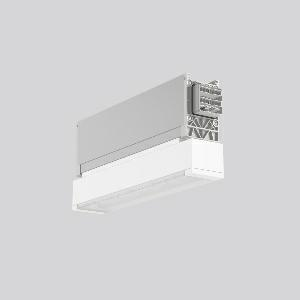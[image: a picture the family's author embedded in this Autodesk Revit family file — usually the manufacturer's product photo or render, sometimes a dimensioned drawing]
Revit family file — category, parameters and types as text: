
# Revit family: linedo_module_rq_9503rq_760_400_0hc_16c4
name_source: partatom
category: Lighting Fixtures
units: mm (PartAtom-declared; Revit-internal decimal feet)

## family parameters
Cut with Voids When Loaded = No
Host = Face
Light Source = No
Part Type = Normal
Room Calculation Point = No
Round Connector Dimension = Use Diameter
Shared = No

## types (1)
- LINEDO Module RQ (1 x LED Modul 763, 390 lm, 6300)
    Apparent Load = 6 VA
    CIE Flux Codes = 39 72 97 99 100
    Color Rendering = 70
    Color Temperature = 6300
    Default Elevation = 1800 mm
    Description = LINEDO, 5,5 W, 390 lm, 763, aluminium, on/off
Continuous line luminaire, L 342 B 58 H 147, CBS, emergency-390 lm, Stromkreis
Project solution!
    Height = 147 mm
    Lamp = 1 x LED Modul 763
    Lamp Light Flux = 390 lm
    Lamp count = 1
    Length = 342 mm
    Lifetime = 50000 h
    Luminous efficacy = 71 lm/W
    Manufacturer = RZB
    ModVariant = No
    Model = 9503RQ.760.400.0HC
    Mounting Place = Ceiling
    Mounting Type = Surface mounted
    Number of Poles = 1
    OnlyDefault = Yes
    Power Factor = 1
    Product Name = LINEDO Module RQ
    Product group = Continuous line luminaire system Linedo IP 54
    ProductGroupID = 314
    Protection Class = Protection class I
    Protection Degree = IP 54
    RLX_Detail_Level = 1
    RLX_Emergency_Light_Flux = 390 lm
    RLX_Emergency_Type = 3
    RLX_Emergency_Type_DB = Yes
    RlxData = <blob elided: 34273 chars, md5=7489cbff>
    Socket = socket
    Standby Power = 0 W
    System Light Flux = 390 lm
    System Power = 6 W
    Type Comments = Product without accessories
    Type Image = 9503rf.760.430.0hc.jpg
    URL = http://relux.com
    VarID = ---
    Voltage = 230 V
    Voltage Range = 220-240 V
    Weight = 0.00 kg
    Width = 58 mm

## geometry (parser evidence)
native form markers: Blend x4, Sweep x11
no freeform markers — native parametric forms only
